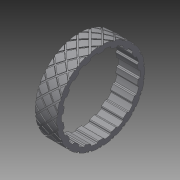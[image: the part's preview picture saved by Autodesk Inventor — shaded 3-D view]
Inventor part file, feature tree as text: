
AUTODESK INVENTOR PART (.ipt)
format: ipt  version: 2013 (Build 170138000, 138)  size: 784,384 bytes
history: native  units: in
note: dims shown in document units (in); Inventor stores cm internally (conversion verified against a paired STEP export)
features: mirror x1, imported_body x1
ambient origin geometry x8: Origin, YZ Plane, XZ Plane, XY Plane, X Axis, Y Axis, Z Axis, Center Point
feature tree (2):
  mirror  "Mirror1"
  imported_body  "Base1"
